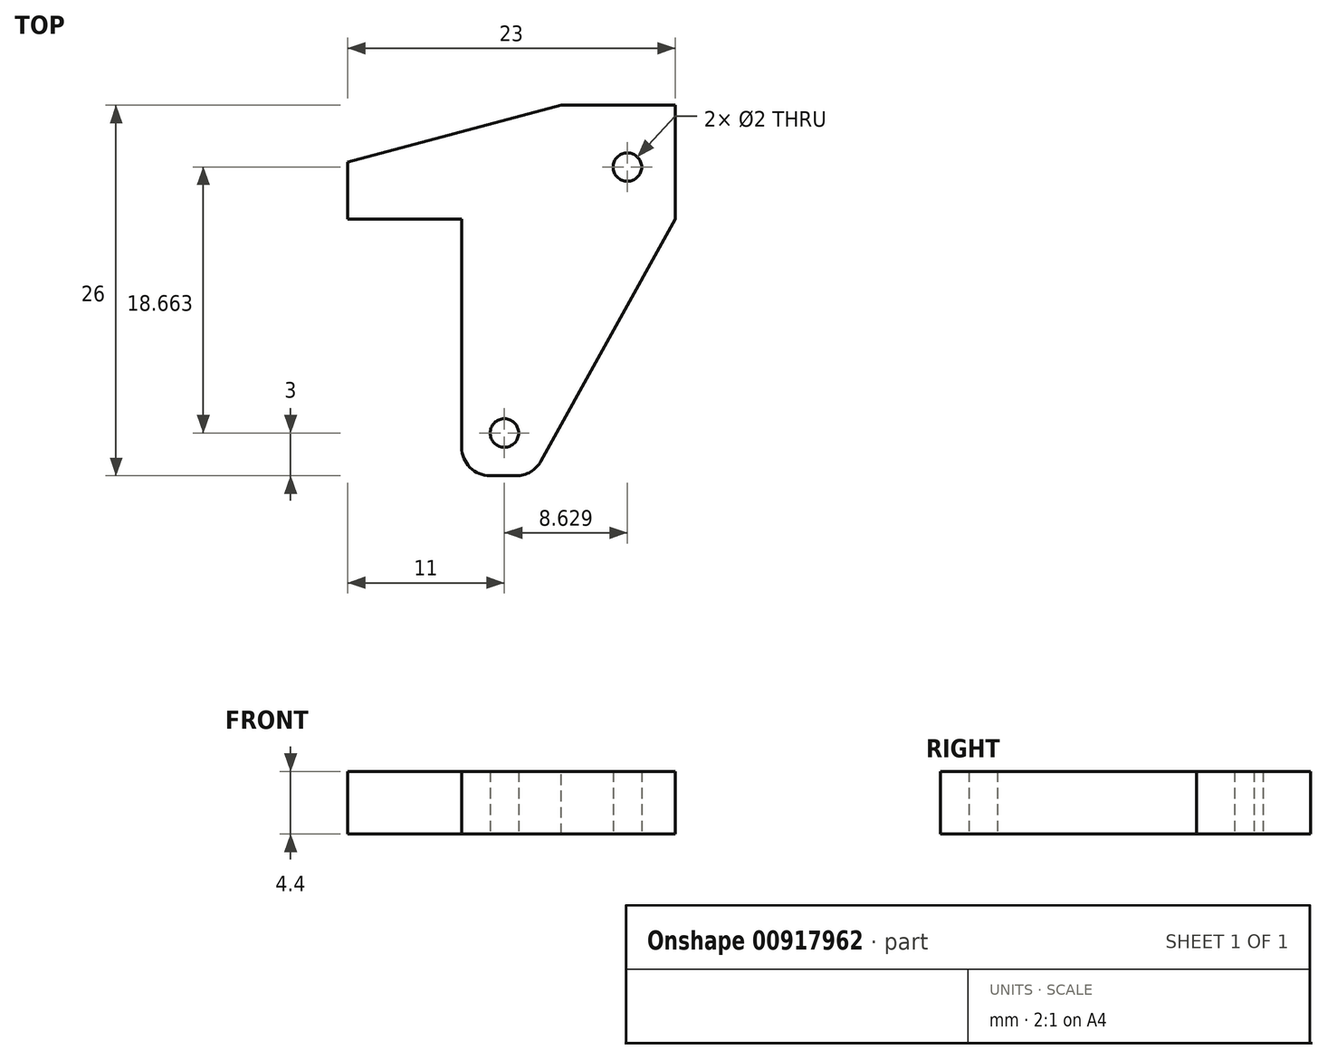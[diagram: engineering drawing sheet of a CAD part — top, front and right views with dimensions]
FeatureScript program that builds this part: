
annotation { "Feature Type Name" : "Feature", "Feature Type Description" : "" }
export const myFeature = defineFeature(function(context is Context, id is Id, definition is map)
    precondition{}
    {
        {
            var Q0;
            Q0=qCreatedBy(makeId("Top.planeOp"),FACE);
            var sketch = newSketch(context, id + "F0", { "sketchPlane" : qUnion([Q0])});
            skLineSegment(sketch, "E0.bottom", {"start": v(0, 0) * mm, "end": v(15, 0) * mm});
            skLineSegment(sketch, "E0.top", {"start": v(0, 18) * mm, "end": v(15, 18) * mm});
            skLineSegment(sketch, "E0.left", {"start": v(0, 0) * mm, "end": v(0, 18) * mm});
            skLineSegment(sketch, "E0.right", {"start": v(15, 0) * mm, "end": v(15, 18) * mm});
            skSolve(sketch);
        }
        {
            var Q0;
            Q0=makeQuery(id+"F0.imprint","IMPRINT",FACE,{"disambiguationData":[TD([[makeQuery(id+"F0.imprint","IMPRINT",EDGE,{"derivedFrom":sQuery(id+"F0.wireOp",EDGE,"E0.bottom")}),1.0]])]});
            extrude(context, id + "F1", {"entities" : qUnion([Q0]), "depth" : 4.4 * mm, "offsetDistance" : 25 * mm});
        }
        {
            var Q0;
            Q0=makeQuery(id+"F1.opExtrude","SWEPT_EDGE",EDGE,{"disambiguationData":[OSD([sQuery(id+"F0.wireOp",EDGE,"E0.bottom"),sQuery(id+"F0.wireOp",EDGE,"E0.left")])]});
            fillet(context, id + "F2", {"entities" : qUnion([Q0]), "radius" : 2 * mm, "tangentPropagation" : true, "allowEdgeOverflow" : false});
        }
        {
            var Q0;
            Q0=makeQuery(id+"F1.opExtrude","SWEPT_EDGE",EDGE,{"disambiguationData":[OSD([sQuery(id+"F0.wireOp",EDGE,"E0.bottom"),sQuery(id+"F0.wireOp",EDGE,"E0.right")])]});
            chamfer(context, id + "F3", {"entities" : qUnion([Q0]), "chamferType" : ChamferType.TWO_OFFSETS, "width1" : 18 * mm, "oppositeDirection" : false, "width2" : 10 * mm, "tangentPropagation" : true});
        }
        {
            var Q0;
            {var subQ0=sQuery(id+"F0.wireOp",EDGE,"E0.bottom");Q0=makeQuery(id+"F3.opChamfer","BLEND_EDGE",EDGE,{"blendedFrom":[makeQuery(id+"F1.opExtrude","SWEPT_EDGE",EDGE,{"disambiguationData":[OSD([subQ0,sQuery(id+"F0.wireOp",EDGE,"E0.right")])]}),makeQuery(id+"F1.opExtrude","SWEPT_FACE",FACE,{"disambiguationData":[OSD([subQ0])]})],"blendedInto":[makeQuery(id+"F1.opExtrude","SWEPT_FACE",FACE,{"disambiguationData":[OSD([subQ0])]})]});}
            fillet(context, id + "F4", {"entities" : qUnion([Q0]), "radius" : 2 * mm, "tangentPropagation" : true, "allowEdgeOverflow" : false});
        }
        {
            var Q0;
            Q0=makeQuery(id+"F1.opExtrude","CAP_FACE",FACE,{"disambiguationData":[OSD([sQuery(id+"F0.wireOp",EDGE,"E0.bottom"),sQuery(id+"F0.wireOp",EDGE,"E0.top"),sQuery(id+"F0.wireOp",EDGE,"E0.left"),sQuery(id+"F0.wireOp",EDGE,"E0.right")])],"isStart":true});
            var sketch = newSketch(context, id + "F5", { "sketchPlane" : qUnion([Q0])});
            skLineSegment(sketch, "E1", {"start": v(3, 0) * mm, "end": v(3, -3) * mm, "construction": true});
            skCircle(sketch, "E2", {"center": v(3, -3) * mm, "radius": 1 * mm});
            skLineSegment(sketch, "E3", {"start": v(3, -3) * mm, "end": v(0, -3) * mm});
            skSolve(sketch);
        }
        {
            var Q0;
            Q0=makeQuery(id+"F1.opExtrude","SWEPT_FACE",FACE,{"disambiguationData":[OSD([sQuery(id+"F0.wireOp",EDGE,"E0.top")])]});
            var sketch = newSketch(context, id + "F6", { "sketchPlane" : qUnion([Q0])});
            skLineSegment(sketch, "E4.bottom", {"start": v(0, 4.4) * mm, "end": v(8, 4.4) * mm});
            skLineSegment(sketch, "E4.top", {"start": v(0, 0) * mm, "end": v(8, 0) * mm});
            skLineSegment(sketch, "E4.left", {"start": v(0, 4.4) * mm, "end": v(0, 0) * mm});
            skLineSegment(sketch, "E4.right", {"start": v(8, 4.4) * mm, "end": v(8, 0) * mm});
            skSolve(sketch);
        }
        {
            var Q0;
            Q0=makeQuery(id+"F6.imprint","IMPRINT",FACE,{"disambiguationData":[TD([[makeQuery(id+"F6.imprint","IMPRINT",EDGE,{"derivedFrom":sQuery(id+"F6.wireOp",EDGE,"E4.bottom")}),-1.0]])]});
            var Q1;
            Q1=makeQuery(id+"F6.imprint","IMPRINT",FACE,{"disambiguationData":[TD([[makeQuery(id+"F6.imprint","IMPRINT",EDGE,{"derivedFrom":sQuery(id+"F6.wireOp",EDGE,"E4.left")}),-1.0]])]});
            extrude(context, id + "F7", {"entities" : qUnion([Q0, Q1]), "operationType" : NewBodyOperationType.ADD, "depth" : 4 * mm, "offsetDistance" : 25 * mm});
        }
        {
            var Q0;
            Q0=makeQuery(id+"F7.opExtrude","CAP_FACE",FACE,{"disambiguationData":[OSD([sQuery(id+"F0.wireOp",EDGE,"E0.bottom"),sQuery(id+"F0.wireOp",EDGE,"E0.top"),sQuery(id+"F0.wireOp",EDGE,"E0.right"),sQuery(id+"F6.wireOp",EDGE,"E4.bottom"),sQuery(id+"F6.wireOp",EDGE,"E4.top"),sQuery(id+"F6.wireOp",EDGE,"E4.right")])],"isStart":false});
            extrude(context, id + "F8", {"entities" : qUnion([Q0]), "operationType" : NewBodyOperationType.ADD, "depth" : 4 * mm, "offsetDistance" : 25 * mm});
        }
        {
            var Q0;
            Q0=makeQuery(id+"F8.opExtrude","CAP_EDGE",EDGE,{"disambiguationData":[OSD([sQuery(id+"F6.wireOp",EDGE,"E4.right")])],"isStart":false});
            chamfer(context, id + "F9", {"entities" : qUnion([Q0]), "chamferType" : ChamferType.TWO_OFFSETS, "width1" : 4 * mm, "oppositeDirection" : false, "width2" : 15 * mm, "tangentPropagation" : true});
        }
        {
            var Q0;
            Q0=makeQuery(id+"F5.imprint","IMPRINT",FACE,{"disambiguationData":[TD([[makeQuery(id+"F5.imprint","IMPRINT",EDGE,{"derivedFrom":sQuery(id+"F5.wireOp",EDGE,"E2")}),1.0]])]});
            var Q1;
            Q1=sQuery(id+"F5.wireOp",EDGE,"E2");
            extrude(context, id + "F10", {"entities" : qUnion([Q0]), "operationType" : NewBodyOperationType.REMOVE, "surfaceEntities" : qUnion([Q1]), "oppositeDirection" : true, "depth" : 4.4 * mm, "offsetDistance" : 25 * mm});
        }
        {
            var Q0;
            {var subQ0=sQuery(id+"F6.wireOp",EDGE,"E4.top");var subQ1=sQuery(id+"F0.wireOp",EDGE,"E0.top");Q0=makeQuery(id+"F8.boolean.opBoolean","MERGE",FACE,{"derivedFrom":[makeQuery(id+"F7.boolean.opBoolean","MERGE",FACE,{"derivedFrom":[makeQuery(id+"F1.opExtrude","CAP_FACE",FACE,{"disambiguationData":[OSD([sQuery(id+"F0.wireOp",EDGE,"E0.bottom"),subQ1,sQuery(id+"F0.wireOp",EDGE,"E0.left"),sQuery(id+"F0.wireOp",EDGE,"E0.right")])],"isStart":true}),makeQuery(id+"F7.opExtrude","SWEPT_FACE",FACE,{"disambiguationData":[OSD([subQ1,subQ0])]})]}),makeQuery(id+"F8.opExtrude","SWEPT_FACE",FACE,{"disambiguationData":[OSD([subQ1,subQ0])]})]});}
            var sketch = newSketch(context, id + "F11", { "sketchPlane" : qUnion([Q0])});
            skCircle(sketch, "E5", {"center": v(11.63, -21.66) * mm, "radius": 1 * mm});
            skSolve(sketch);
        }
        {
            var Q0;
            Q0=makeQuery(id+"F11.imprint","IMPRINT",FACE,{"disambiguationData":[TD([[makeQuery(id+"F11.imprint","IMPRINT",EDGE,{"derivedFrom":sQuery(id+"F11.wireOp",EDGE,"E5")}),1.0]])]});
            extrude(context, id + "F12", {"entities" : qUnion([Q0]), "operationType" : NewBodyOperationType.REMOVE, "oppositeDirection" : true, "depth" : 4.4 * mm, "offsetDistance" : 25 * mm});
        }
    });
